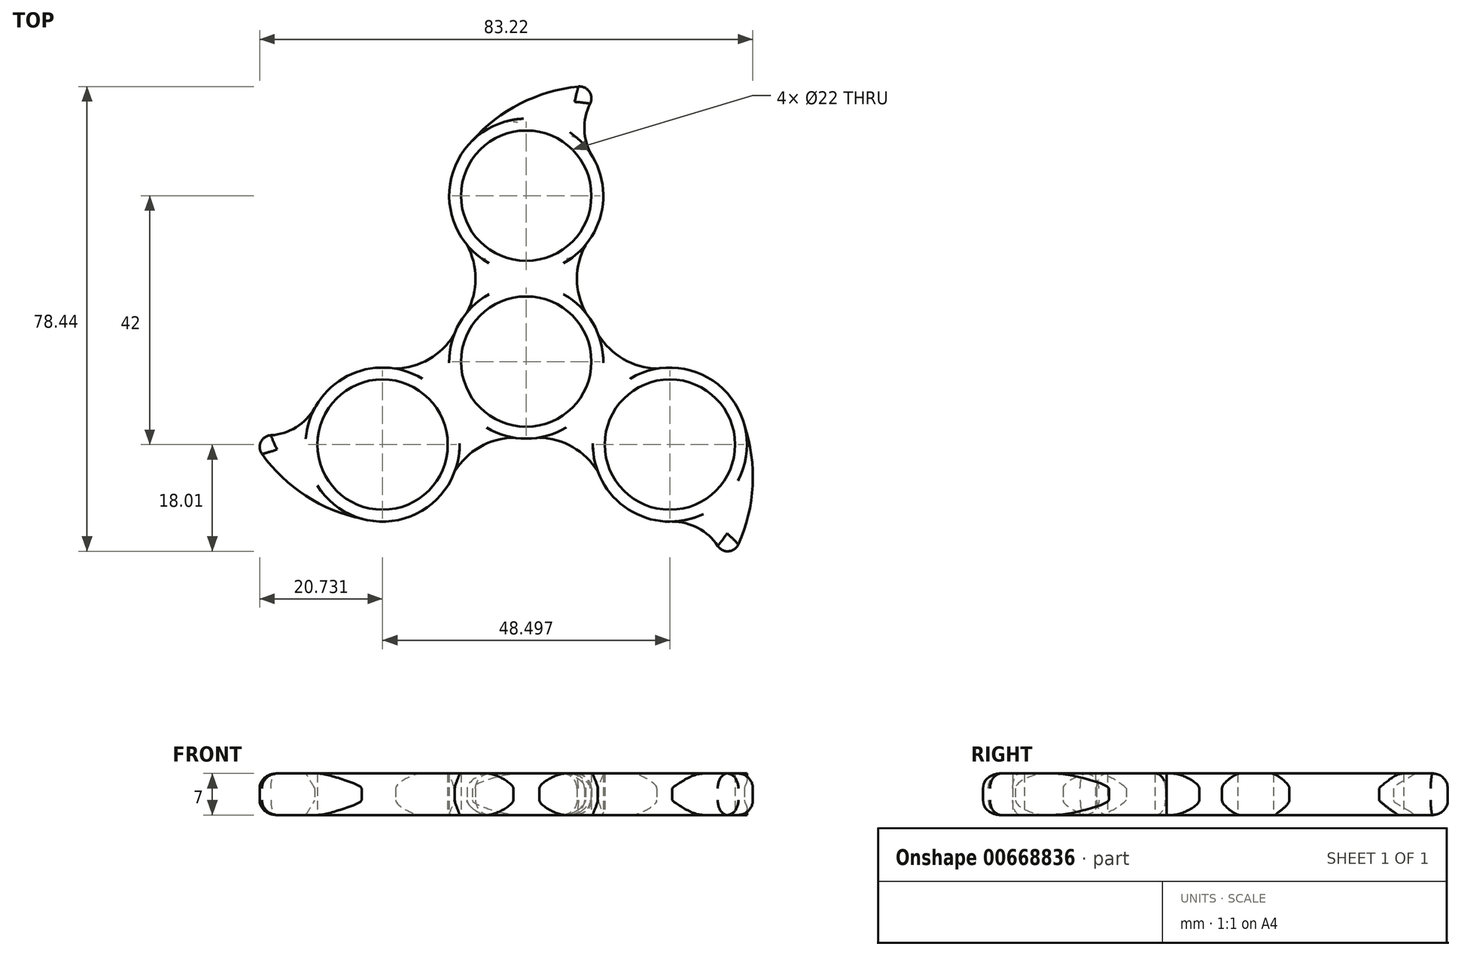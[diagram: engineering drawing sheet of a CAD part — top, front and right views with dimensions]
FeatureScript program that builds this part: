
annotation { "Feature Type Name" : "Feature", "Feature Type Description" : "" }
export const myFeature = defineFeature(function(context is Context, id is Id, definition is map)
    precondition{}
    {
        {
            var Q0;
            Q0=qCreatedBy(makeId("Top.planeOp"),FACE);
            var sketch = newSketch(context, id + "F0", { "sketchPlane" : qUnion([Q0])});
            skCircle(sketch, "E0", {"center": v(0, 0) * mm, "radius": 11 * mm});
            skCircle(sketch, "E1", {"center": v(0, 28) * mm, "radius": 11 * mm});
            skArc(sketch, "E2", {"start": v(-10, 8.3) * mm, "mid": v(0, -13) * mm, "end": v(10, 8.3) * mm});
            skArc(sketch, "E3", {"start": v(10, 19.7) * mm, "mid": v(0, 41) * mm, "end": v(-10, 19.7) * mm});
            skArc(sketch, "E4", {"start": v(10, 19.7) * mm, "mid": v(8.56, 14) * mm, "end": v(10, 8.3) * mm});
            skArc(sketch, "E5", {"start": v(-10, 8.3) * mm, "mid": v(-8.56, 14) * mm, "end": v(-10, 19.7) * mm});
            skSolve(sketch);
        }
        {
            var Q0;
            Q0=makeQuery(id+"F0.imprint","IMPRINT",FACE,{"disambiguationData":[TD([[makeQuery(id+"F0.imprint","IMPRINT",EDGE,{"derivedFrom":sQuery(id+"F0.wireOp",EDGE,"E0")}),-1.0]])]});
            extrude(context, id + "F1", {"entities" : qUnion([Q0]), "depth" : 7 * mm, "offsetDistance" : 25 * mm});
        }
        {
            var Q0;
            Q0=qCreatedBy(makeId("Top.planeOp"),FACE);
            var sketch = newSketch(context, id + "F2", { "sketchPlane" : qUnion([Q0])});
            skArc(sketch, "E6", {"start": v(11.05, 34.84) * mm, "mid": v(1.56, 40.9) * mm, "end": v(-9.1, 37.28) * mm});
            skArc(sketch, "E7", {"start": v(9.5, 46.48) * mm, "mid": v(-0.7, 43.69) * mm, "end": v(-9.1, 37.28) * mm});
            skArc(sketch, "E8", {"start": v(12.67, 46.07) * mm, "mid": v(9.9, 40.74) * mm, "end": v(11.05, 34.84) * mm});
            skArc(sketch, "E9.trimOffspring", {"start": v(12.67, 46.07) * mm, "mid": v(10.9, 46.45) * mm, "end": v(9.1, 46.45) * mm});
            skSolve(sketch);
        }
        {
            var Q0;
            {var subQ2=sQuery(id+"F2.wireOp",EDGE,"E6");Q0=makeQuery(id+"F2.imprint","IMPRINT",FACE,{"disambiguationData":[TD([[makeQuery(id+"F2.imprint","IMPRINT",EDGE,{"derivedFrom":subQ2}),-1.0]])]});}
            extrude(context, id + "F3", {"entities" : qUnion([Q0]), "operationType" : NewBodyOperationType.ADD, "depth" : 7 * mm, "offsetDistance" : 25 * mm});
        }
        {
            var Q0;
            Q0=makeQuery(id+"F1.opExtrude","SWEPT_BODY",BODY,{"disambiguationData":[OSD([sQuery(id+"F0.wireOp",EDGE,"E0"),sQuery(id+"F0.wireOp",EDGE,"E1"),sQuery(id+"F0.wireOp",EDGE,"E2"),sQuery(id+"F0.wireOp",EDGE,"E3"),sQuery(id+"F0.wireOp",EDGE,"E4"),sQuery(id+"F0.wireOp",EDGE,"E5")])]});
            var Q1;
            Q1=makeQuery(id+"F1.opExtrude","SWEPT_FACE",FACE,{"disambiguationData":[OSD([sQuery(id+"F0.wireOp",EDGE,"E0")])]});
            circularPattern(context, id + "F4", {"operationType" : NewBodyOperationType.ADD, "entities" : qUnion([Q0]), "axis" : qUnion([Q1]), "angle" : 360 * degree, "instanceCount" : 3, "equalSpace" : true});
        }
        {
            var Q0;
            Q0=makeQuery(id+"F4.opPattern","COPY",EDGE,{"derivedFrom":makeQuery(id+"F3.opExtrude","SWEPT_EDGE",EDGE,{"disambiguationData":[OSD([sQuery(id+"F2.wireOp",EDGE,"E8"),sQuery(id+"F2.wireOp",EDGE,"E9.trimOffspring")])]}),"instanceName":"2"});
            var Q1;
            Q1=makeQuery(id+"F4.opPattern","COPY",EDGE,{"derivedFrom":makeQuery(id+"F3.opExtrude","SWEPT_EDGE",EDGE,{"disambiguationData":[OSD([sQuery(id+"F2.wireOp",EDGE,"E8"),sQuery(id+"F2.wireOp",EDGE,"E9.trimOffspring")])]}),"instanceName":"1"});
            var Q2;
            Q2=makeQuery(id+"F3.opExtrude","SWEPT_EDGE",EDGE,{"disambiguationData":[OSD([sQuery(id+"F2.wireOp",EDGE,"E8"),sQuery(id+"F2.wireOp",EDGE,"E9.trimOffspring")])]});
            fillet(context, id + "F5", {"entities" : qUnion([Q0, Q1, Q2]), "radius" : 2 * mm, "tangentPropagation" : true, "allowEdgeOverflow" : false});
        }
        {
            var Q0;
            Q0=makeQuery(id+"F4.opPattern","COPY",EDGE,{"derivedFrom":makeQuery(id+"F1.opExtrude","CAP_EDGE",EDGE,{"disambiguationData":[OSD([sQuery(id+"F0.wireOp",EDGE,"E4")])],"isStart":true}),"instanceName":"1"});
            var Q1;
            Q1=makeQuery(id+"F1.opExtrude","CAP_EDGE",EDGE,{"disambiguationData":[OSD([sQuery(id+"F0.wireOp",EDGE,"E5")])],"isStart":true});
            var Q2;
            Q2=makeQuery(id+"F1.opExtrude","CAP_EDGE",EDGE,{"disambiguationData":[OSD([sQuery(id+"F0.wireOp",EDGE,"E4")])],"isStart":true});
            var Q3;
            Q3=makeQuery(id+"F4.opPattern","COPY",EDGE,{"derivedFrom":makeQuery(id+"F1.opExtrude","CAP_EDGE",EDGE,{"disambiguationData":[OSD([sQuery(id+"F0.wireOp",EDGE,"E5")])],"isStart":true}),"instanceName":"2"});
            var Q4;
            Q4=makeQuery(id+"F4.opPattern","COPY",EDGE,{"derivedFrom":makeQuery(id+"F1.opExtrude","CAP_EDGE",EDGE,{"disambiguationData":[OSD([sQuery(id+"F0.wireOp",EDGE,"E4")])],"isStart":true}),"instanceName":"2"});
            var Q5;
            Q5=makeQuery(id+"F4.opPattern","COPY",EDGE,{"derivedFrom":makeQuery(id+"F1.opExtrude","CAP_EDGE",EDGE,{"disambiguationData":[OSD([sQuery(id+"F0.wireOp",EDGE,"E5")])],"isStart":true}),"instanceName":"1"});
            var Q6;
            Q6=makeQuery(id+"F4.opPattern","COPY",EDGE,{"derivedFrom":makeQuery(id+"F3.opExtrude","CAP_EDGE",EDGE,{"disambiguationData":[OSD([sQuery(id+"F2.wireOp",EDGE,"E8")])],"isStart":true}),"instanceName":"1"});
            var Q7;
            Q7=makeQuery(id+"F3.opExtrude","CAP_EDGE",EDGE,{"disambiguationData":[OSD([sQuery(id+"F2.wireOp",EDGE,"E8")])],"isStart":true});
            var Q8;
            Q8=makeQuery(id+"F4.opPattern","COPY",EDGE,{"derivedFrom":makeQuery(id+"F3.opExtrude","CAP_EDGE",EDGE,{"disambiguationData":[OSD([sQuery(id+"F2.wireOp",EDGE,"E8")])],"isStart":true}),"instanceName":"2"});
            var Q9;
            Q9=makeQuery(id+"F4.opPattern","COPY",EDGE,{"derivedFrom":makeQuery(id+"F3.opExtrude","CAP_EDGE",EDGE,{"disambiguationData":[OSD([sQuery(id+"F2.wireOp",EDGE,"E8")])],"isStart":false}),"instanceName":"1"});
            var Q10;
            Q10=makeQuery(id+"F4.opPattern","COPY",EDGE,{"derivedFrom":makeQuery(id+"F1.opExtrude","CAP_EDGE",EDGE,{"disambiguationData":[OSD([sQuery(id+"F0.wireOp",EDGE,"E4")])],"isStart":false}),"instanceName":"1"});
            var Q11;
            Q11=makeQuery(id+"F1.opExtrude","CAP_EDGE",EDGE,{"disambiguationData":[OSD([sQuery(id+"F0.wireOp",EDGE,"E5")])],"isStart":false});
            var Q12;
            Q12=makeQuery(id+"F3.opExtrude","CAP_EDGE",EDGE,{"disambiguationData":[OSD([sQuery(id+"F2.wireOp",EDGE,"E8")])],"isStart":false});
            var Q13;
            Q13=makeQuery(id+"F1.opExtrude","CAP_EDGE",EDGE,{"disambiguationData":[OSD([sQuery(id+"F0.wireOp",EDGE,"E4")])],"isStart":false});
            var Q14;
            Q14=makeQuery(id+"F4.opPattern","COPY",EDGE,{"derivedFrom":makeQuery(id+"F1.opExtrude","CAP_EDGE",EDGE,{"disambiguationData":[OSD([sQuery(id+"F0.wireOp",EDGE,"E5")])],"isStart":false}),"instanceName":"2"});
            var Q15;
            Q15=makeQuery(id+"F4.opPattern","COPY",EDGE,{"derivedFrom":makeQuery(id+"F1.opExtrude","CAP_EDGE",EDGE,{"disambiguationData":[OSD([sQuery(id+"F0.wireOp",EDGE,"E4")])],"isStart":false}),"instanceName":"2"});
            var Q16;
            Q16=makeQuery(id+"F4.opPattern","COPY",EDGE,{"derivedFrom":makeQuery(id+"F3.opExtrude","CAP_EDGE",EDGE,{"disambiguationData":[OSD([sQuery(id+"F2.wireOp",EDGE,"E8")])],"isStart":false}),"instanceName":"2"});
            var Q17;
            Q17=makeQuery(id+"F4.opPattern","COPY",EDGE,{"derivedFrom":makeQuery(id+"F1.opExtrude","CAP_EDGE",EDGE,{"disambiguationData":[OSD([sQuery(id+"F0.wireOp",EDGE,"E5")])],"isStart":false}),"instanceName":"1"});
            fillet(context, id + "F6", {"entities" : qUnion([Q0, Q1, Q2, Q3, Q4, Q5, Q6, Q7, Q8, Q9, Q10, Q11, Q12, Q13, Q14, Q15, Q16, Q17]), "radius" : 2.5 * mm, "tangentPropagation" : true, "allowEdgeOverflow" : false});
        }
        {
            var Q0;
            {var subQ1=sQuery(id+"F0.wireOp",EDGE,"E5");var subQ2=sQuery(id+"F0.wireOp",EDGE,"E3");Q0=makeQuery(id+"F3.boolean.opBoolean","SPLIT",EDGE,{"disambiguationData":[TD([makeQuery(id+"F1.opExtrude","SWEPT_FACE",FACE,{"disambiguationData":[OSD([subQ1])]})])],"derivedFrom":makeQuery(id+"F1.opExtrude","CAP_EDGE",EDGE,{"disambiguationData":[OSD([subQ2])],"isStart":true})});}
            var Q1;
            {var subQ1=sQuery(id+"F0.wireOp",EDGE,"E3");var subQ2=sQuery(id+"F0.wireOp",EDGE,"E4");Q1=makeQuery(id+"F3.boolean.opBoolean","SPLIT",EDGE,{"disambiguationData":[TD([makeQuery(id+"F1.opExtrude","SWEPT_FACE",FACE,{"disambiguationData":[OSD([subQ2])]})])],"derivedFrom":makeQuery(id+"F1.opExtrude","CAP_EDGE",EDGE,{"disambiguationData":[OSD([subQ1])],"isStart":true})});}
            fillet(context, id + "F7", {"entities" : qUnion([Q0, Q1]), "radius" : .5 * mm, "tangentPropagation" : true, "allowEdgeOverflow" : false});
        }
    });
